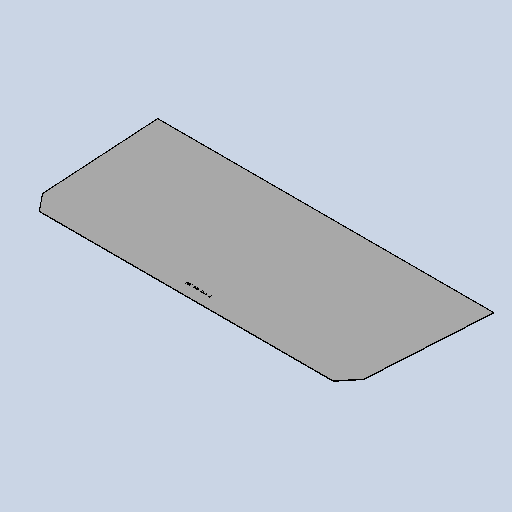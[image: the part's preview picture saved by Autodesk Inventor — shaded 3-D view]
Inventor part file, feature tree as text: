
AUTODESK INVENTOR PART (.ipt)
format: ipt  version: 2025 (Build 290162010, 162A)  size: 176,128 bytes
history: native  units: mm
features: other x6, sketch x2, reference x2, sheet_metal_op x1, mirror x1
ambient origin geometry x8: Origin, YZ Plane, XZ Plane, XY Plane, X Axis, Y Axis, Z Axis, Center Point
bodies: Solid1 (feature_tree)
feature tree (12):
  sheet_metal_op  "Face1"
  mirror  "Mirror1"
  other  "Mark1"
  sketch  "Sketch1"  dims[d2=2.0mm]
  other  "Plate1"
  reference  "Reference3"
  reference  "Reference5"
  sketch  "Sketch2"  dims[d3=10.0mm d4=10.0mm d5=10.0mm d6=12.0mm d7=110.0mm d8=50.0mm]
  other  "ASY MSC 001 отстойник осветлитель.iam"
  other  "ASY MSC 202 LEFT BOARD:1"
  other  "MSC 027 sheet board face 1.ipt:1"
  other  "Definition1"
